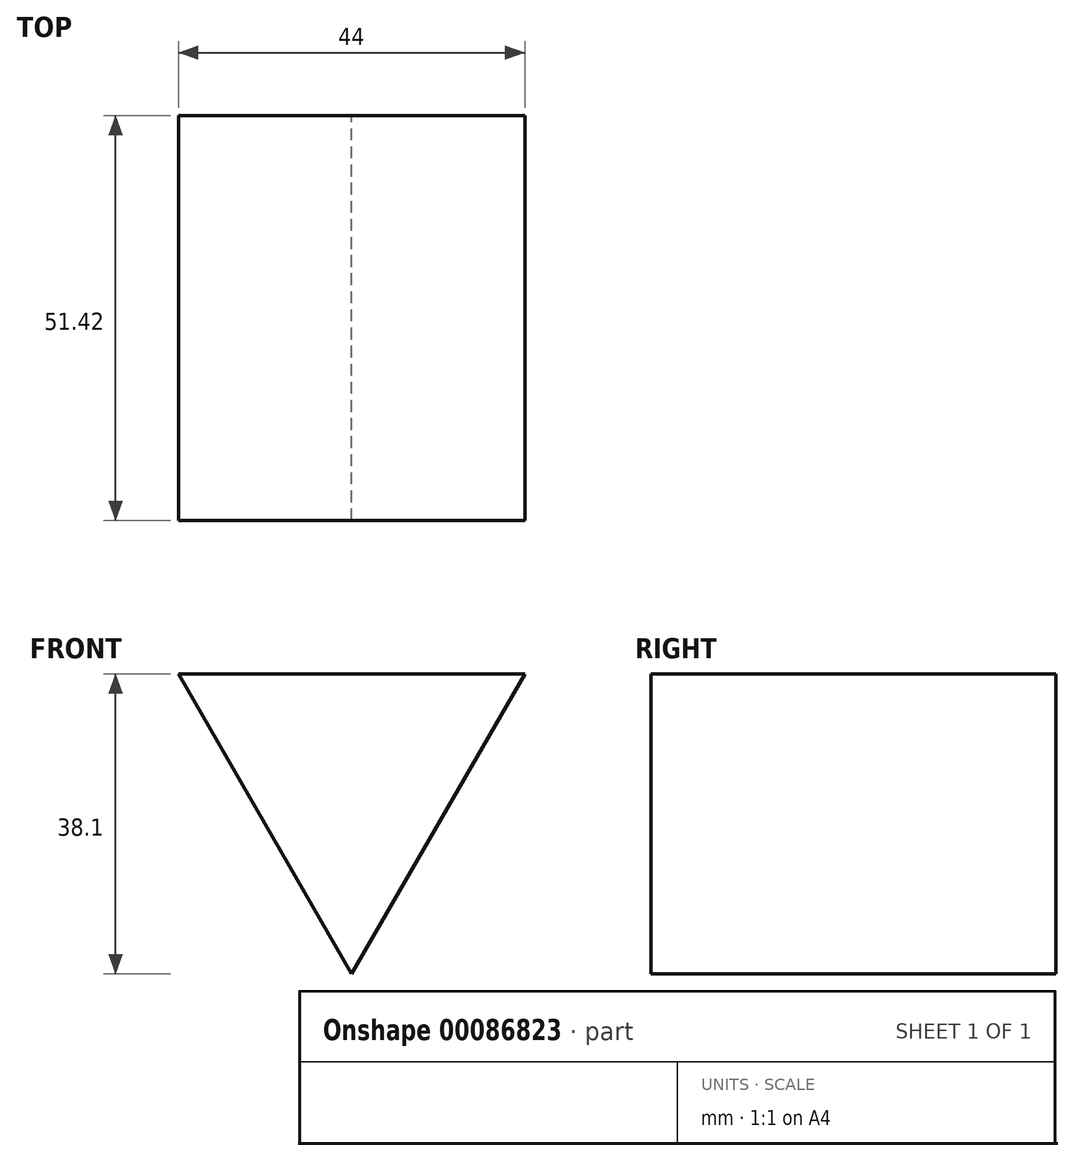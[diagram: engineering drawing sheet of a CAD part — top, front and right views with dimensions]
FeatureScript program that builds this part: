
annotation { "Feature Type Name" : "Feature", "Feature Type Description" : "" }
export const myFeature = defineFeature(function(context is Context, id is Id, definition is map)
    precondition{}
    {
        {
            var Q0;
            Q0=qCreatedBy(makeId("Front.planeOp"),FACE);
            var sketch = newSketch(context, id + "F0", { "sketchPlane" : qUnion([Q0])});
            skCircle(sketch, "E0.cCircle", {"center": v(0, 0) * mm, "radius": 12.7 * mm, "construction": true});
            skLineSegment(sketch, "E0.0", {"start": v(-22, 12.7) * mm, "end": v(22, 12.7) * mm});
            skLineSegment(sketch, "E0.1", {"start": v(22, 12.7) * mm, "end": v(0, -25.4) * mm});
            skLineSegment(sketch, "E0.2", {"start": v(0, -25.4) * mm, "end": v(-22, 12.7) * mm});
            skPoint(sketch, "E0.0.midPoint", {"position": v(0, 12.7) * mm});
            skSolve(sketch);
        }
        {
            var Q0;
            Q0 = qSketchRegion(id + "F0", true);
            extrude(context, id + "F1", {"entities" : qUnion([Q0]), "depth" : 51.42 * mm});
        }
    });
